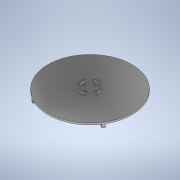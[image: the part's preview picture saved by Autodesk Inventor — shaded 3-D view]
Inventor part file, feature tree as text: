
AUTODESK INVENTOR PART (.ipt)
format: ipt  version: 2021 (Build 250183000, 183)  size: 189,952 bytes
history: native  units: mm
features: sketch x4, extrude x3, revolve x1, thread x1
ambient origin geometry x8: Origin, YZ Plane, XZ Plane, XY Plane, X Axis, Y Axis, Z Axis, Center Point
bodies: Solid1 (feature_tree)
feature tree (9):
  revolve  "Revolution1"  [1 undecoded]
  thread  "Thread1"  [1 undecoded]
  extrude  "Extrusion1"  Depth=3.0mm
  extrude  "Extrusion2"  Depth=60.0mm
  extrude  "Extrusion3"  Depth=5.0mm
  sketch  "Sketch1"  dims[d0=4.0mm d1=6.0mm d2=0.0mm]
  sketch  "Sketch2"  dims[d3=3.0mm d4=2.0mm]
  sketch  "Sketch3"  dims[d7=2.5mm d8=60.0mm]
  sketch  "Sketch5"  dims[d9=13.95mm d10=5.0mm d11=90.0deg d12=8.0mm d13=0.0mm d14=3.0mm d15=3.0mm d16=3.0mm d17=3.0mm d18=19.0mm d19=9.5mm d20=16.0mm d21=8.0mm d22=0.0mm d23=0.0mm d24=40.0mm d26=360.0deg d28=10.0mm d29=0.0mm d32=4.0mm d33=40.0mm d35=360.0deg d37=6.0mm d38=0.0mm]
note: 2 required parameter values undecoded (feature->parameter linkage not recoverable at this tier; creation-order binding heuristic only, values carry confidence <= 0.55)